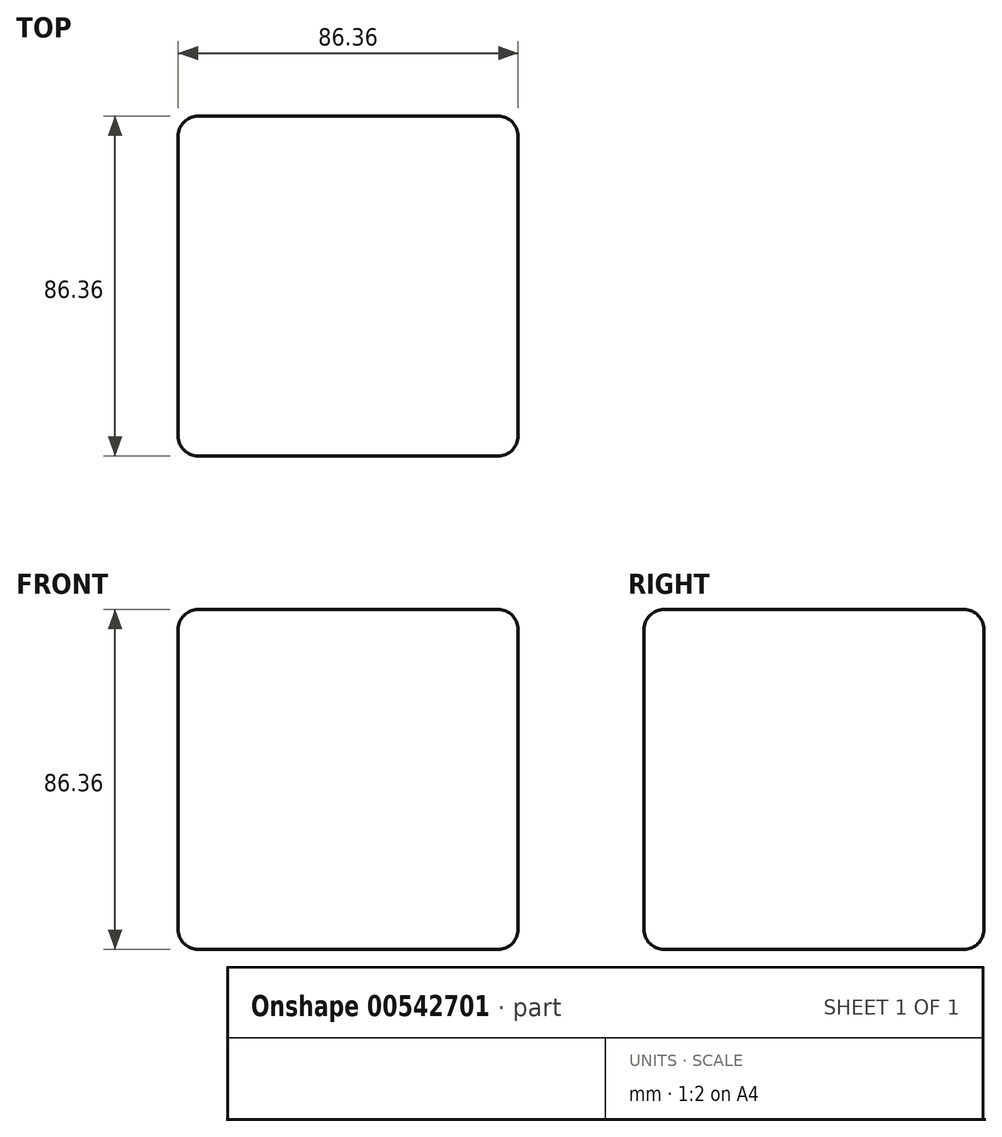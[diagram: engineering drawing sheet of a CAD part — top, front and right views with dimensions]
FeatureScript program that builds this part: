
annotation { "Feature Type Name" : "Feature", "Feature Type Description" : "" }
export const myFeature = defineFeature(function(context is Context, id is Id, definition is map)
    precondition{}
    {
        {
            var Q0;
            Q0=qCreatedBy(makeId("Top.planeOp"),FACE);
            var sketch = newSketch(context, id + "F0", { "sketchPlane" : qUnion([Q0])});
            skLineSegment(sketch, "E0.bottom", {"start": v(0, 0) * mm, "end": v(-43.18, 0) * mm});
            skLineSegment(sketch, "E0.top", {"start": v(0, -43.18) * mm, "end": v(-43.18, -43.18) * mm});
            skLineSegment(sketch, "E0.right", {"start": v(-43.18, 0) * mm, "end": v(-43.18, -43.18) * mm});
            skLineSegment(sketch, "E1.top", {"start": v(0, 43.18) * mm, "end": v(-43.18, 43.18) * mm});
            skLineSegment(sketch, "E1.left", {"start": v(0, 0) * mm, "end": v(0, 43.18) * mm});
            skLineSegment(sketch, "E1.right", {"start": v(-43.18, 0) * mm, "end": v(-43.18, 43.18) * mm});
            skLineSegment(sketch, "E2.bottom", {"start": v(0, 0) * mm, "end": v(43.18, 0) * mm});
            skLineSegment(sketch, "E2.top", {"start": v(0, 43.18) * mm, "end": v(43.18, 43.18) * mm});
            skLineSegment(sketch, "E2.right", {"start": v(43.18, 0) * mm, "end": v(43.18, 43.18) * mm});
            skLineSegment(sketch, "E3", {"start": v(0, -43.18) * mm, "end": v(0, 0) * mm});
            skLineSegment(sketch, "E4.top", {"start": v(0, -43.18) * mm, "end": v(43.18, -43.18) * mm});
            skLineSegment(sketch, "E4.left", {"start": v(0, 0) * mm, "end": v(0, -43.18) * mm});
            skLineSegment(sketch, "E4.right", {"start": v(43.18, 0) * mm, "end": v(43.18, -43.18) * mm});
            skSolve(sketch);
        }
        {
            var Q0;
            Q0=makeQuery(id+"F0.imprint","IMPRINT",FACE,{"disambiguationData":[TD([[makeQuery(id+"F0.imprint","IMPRINT",EDGE,{"derivedFrom":sQuery(id+"F0.wireOp",EDGE,"E0.bottom")}),-1.0]])]});
            var Q1;
            Q1=makeQuery(id+"F0.imprint","IMPRINT",FACE,{"disambiguationData":[TD([[makeQuery(id+"F0.imprint","IMPRINT",EDGE,{"derivedFrom":sQuery(id+"F0.wireOp",EDGE,"E2.bottom")}),-1.0]])]});
            var Q2;
            Q2=makeQuery(id+"F0.imprint","IMPRINT",FACE,{"disambiguationData":[TD([[makeQuery(id+"F0.imprint","IMPRINT",EDGE,{"derivedFrom":sQuery(id+"F0.wireOp",EDGE,"E2.top")}),-1.0]])]});
            var Q3;
            Q3=makeQuery(id+"F0.imprint","IMPRINT",FACE,{"disambiguationData":[TD([[makeQuery(id+"F0.imprint","IMPRINT",EDGE,{"derivedFrom":sQuery(id+"F0.wireOp",EDGE,"E0.top")}),-1.0]])]});
            extrude(context, id + "F1", {"entities" : qUnion([Q0, Q1, Q2, Q3]), "depth" : 86.36 * mm, "offsetDistance" : 25.4 * mm});
        }
        {
            var Q0;
            Q0=makeQuery(id+"F1.opExtrude","CAP_EDGE",EDGE,{"disambiguationData":[OSD([sQuery(id+"F0.wireOp",EDGE,"E0.right"),sQuery(id+"F0.wireOp",EDGE,"E1.right")])],"isStart":false});
            var Q1;
            Q1=makeQuery(id+"F1.opExtrude","CAP_EDGE",EDGE,{"disambiguationData":[OSD([sQuery(id+"F0.wireOp",EDGE,"E1.top"),sQuery(id+"F0.wireOp",EDGE,"E2.top")])],"isStart":false});
            var Q2;
            Q2=makeQuery(id+"F1.opExtrude","SWEPT_EDGE",EDGE,{"disambiguationData":[OSD([sQuery(id+"F0.wireOp",EDGE,"E1.top"),sQuery(id+"F0.wireOp",EDGE,"E1.right")])]});
            var Q3;
            Q3=makeQuery(id+"F1.opExtrude","CAP_EDGE",EDGE,{"disambiguationData":[OSD([sQuery(id+"F0.wireOp",EDGE,"E0.top"),sQuery(id+"F0.wireOp",EDGE,"E4.top")])],"isStart":false});
            var Q4;
            Q4=makeQuery(id+"F1.opExtrude","SWEPT_EDGE",EDGE,{"disambiguationData":[OSD([sQuery(id+"F0.wireOp",EDGE,"E0.top"),sQuery(id+"F0.wireOp",EDGE,"E0.right")])]});
            var Q5;
            Q5=makeQuery(id+"F1.opExtrude","CAP_EDGE",EDGE,{"disambiguationData":[OSD([sQuery(id+"F0.wireOp",EDGE,"E0.right"),sQuery(id+"F0.wireOp",EDGE,"E1.right")])],"isStart":true});
            var Q6;
            Q6=makeQuery(id+"F1.opExtrude","CAP_EDGE",EDGE,{"disambiguationData":[OSD([sQuery(id+"F0.wireOp",EDGE,"E0.top"),sQuery(id+"F0.wireOp",EDGE,"E4.top")])],"isStart":true});
            var Q7;
            Q7=makeQuery(id+"F1.opExtrude","SWEPT_EDGE",EDGE,{"disambiguationData":[OSD([sQuery(id+"F0.wireOp",EDGE,"E4.top"),sQuery(id+"F0.wireOp",EDGE,"E4.right")])]});
            var Q8;
            Q8=makeQuery(id+"F1.opExtrude","CAP_EDGE",EDGE,{"disambiguationData":[OSD([sQuery(id+"F0.wireOp",EDGE,"E2.right"),sQuery(id+"F0.wireOp",EDGE,"E4.right")])],"isStart":false});
            var Q9;
            Q9=makeQuery(id+"F1.opExtrude","SWEPT_EDGE",EDGE,{"disambiguationData":[OSD([sQuery(id+"F0.wireOp",EDGE,"E2.top"),sQuery(id+"F0.wireOp",EDGE,"E2.right")])]});
            var Q10;
            Q10=makeQuery(id+"F1.opExtrude","CAP_EDGE",EDGE,{"disambiguationData":[OSD([sQuery(id+"F0.wireOp",EDGE,"E2.right"),sQuery(id+"F0.wireOp",EDGE,"E4.right")])],"isStart":true});
            var Q11;
            Q11=makeQuery(id+"F1.opExtrude","CAP_EDGE",EDGE,{"disambiguationData":[OSD([sQuery(id+"F0.wireOp",EDGE,"E1.top"),sQuery(id+"F0.wireOp",EDGE,"E2.top")])],"isStart":true});
            fillet(context, id + "F2", {"entities" : qUnion([Q0, Q1, Q2, Q3, Q4, Q5, Q6, Q7, Q8, Q9, Q10, Q11]), "radius" : 5.08 * mm, "tangentPropagation" : true, "allowEdgeOverflow" : false});
        }
    });
